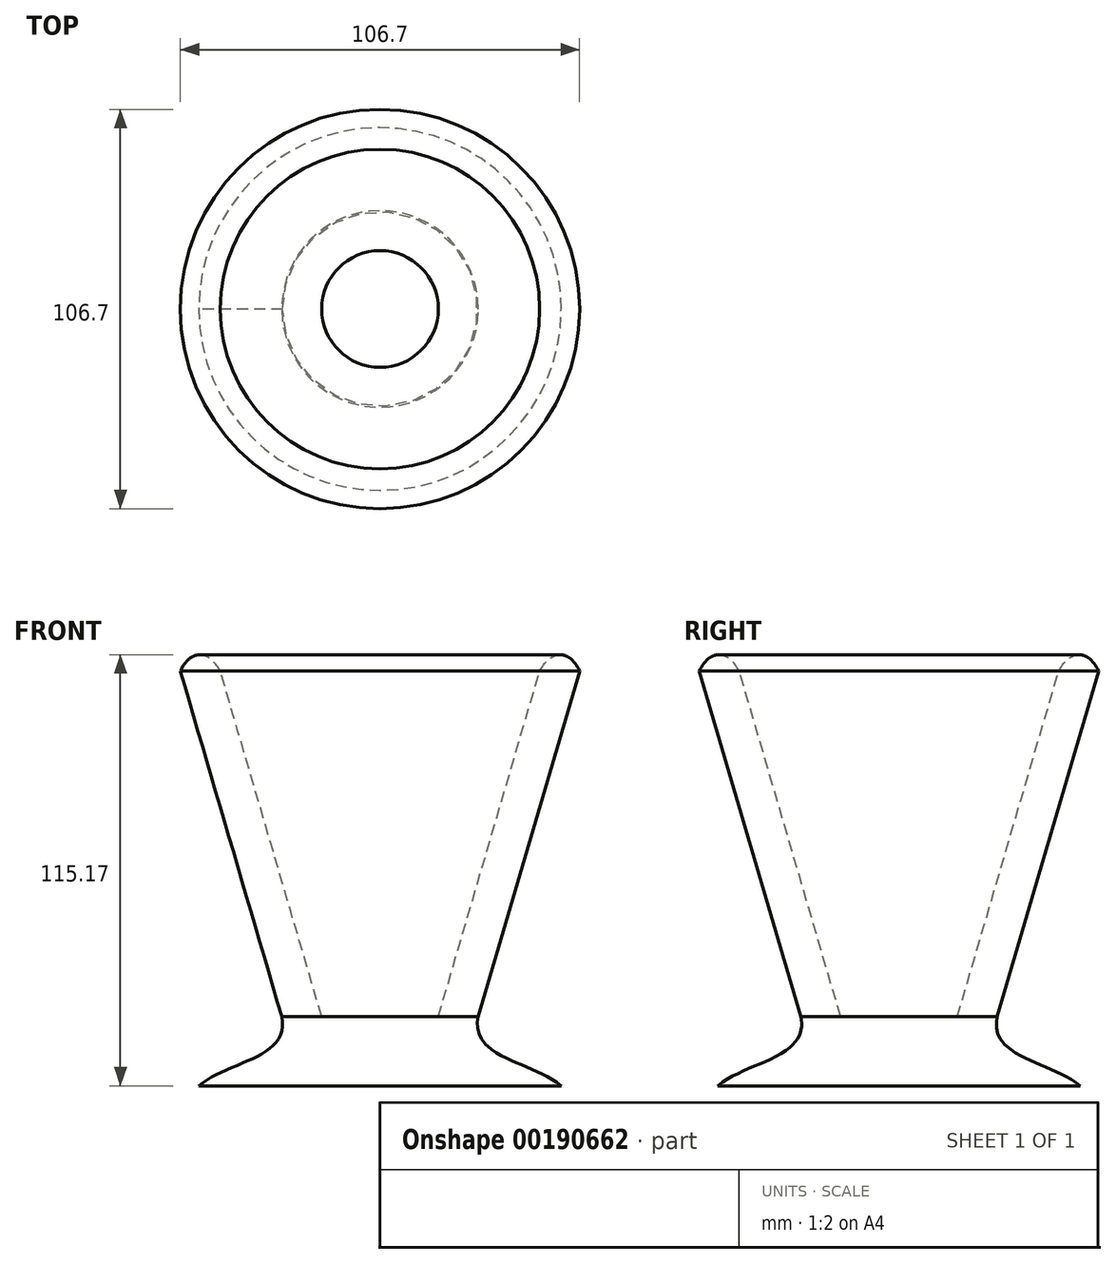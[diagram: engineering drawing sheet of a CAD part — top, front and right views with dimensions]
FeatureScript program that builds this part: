
annotation { "Feature Type Name" : "Feature", "Feature Type Description" : "" }
export const myFeature = defineFeature(function(context is Context, id is Id, definition is map)
    precondition{}
    {
        {
            var Q0;
            Q0=qCreatedBy(makeId("Front.planeOp"),FACE);
            var sketch = newSketch(context, id + "F0", { "sketchPlane" : qUnion([Q0])});
            skLineSegment(sketch, "E0", {"start": v(26.27, -39.8) * mm, "end": v(53.35, 52.53) * mm});
            skFitSpline(sketch, "E1", {"points": [v(26.27, -39.8) * mm, v(48.43, -58.28) * mm], "startDerivative": vector(-7.39, -33.24) * mm, "endDerivative": vector(23.4, -19.7) * mm});
            skLineSegment(sketch, "E2", {"start": v(48.43, -58.28) * mm, "end": v(0, -58.28) * mm});
            skLineSegment(sketch, "E3", {"start": v(0, -58.28) * mm, "end": v(0, -39.8) * mm});
            skLineSegment(sketch, "E4", {"start": v(0, -39.8) * mm, "end": v(15.6, -39.8) * mm});
            skLineSegment(sketch, "E5", {"start": v(15.6, -39.8) * mm, "end": v(42.68, 52.53) * mm});
            skFitSpline(sketch, "E6", {"points": [v(42.68, 52.53) * mm, v(53.35, 52.53) * mm], "startDerivative": vector(12.31, 20.93) * mm, "endDerivative": vector(6.16, -13.54) * mm});
            skSolve(sketch);
        }
        {
            var Q0;
            Q0=makeQuery(id+"F0.imprint","IMPRINT",FACE,{"disambiguationData":[TD([[makeQuery(id+"F0.imprint","IMPRINT",EDGE,{"derivedFrom":sQuery(id+"F0.wireOp",EDGE,"E0")}),1.0]])]});
            var Q1;
            Q1=sQuery(id+"F0.wireOp",EDGE,"E3");
            revolve(context, id + "F1", {"entities" : qUnion([Q0]), "axis" : qUnion([Q1]), "revolveType" : RevolveType.FULL});
        }
    });
